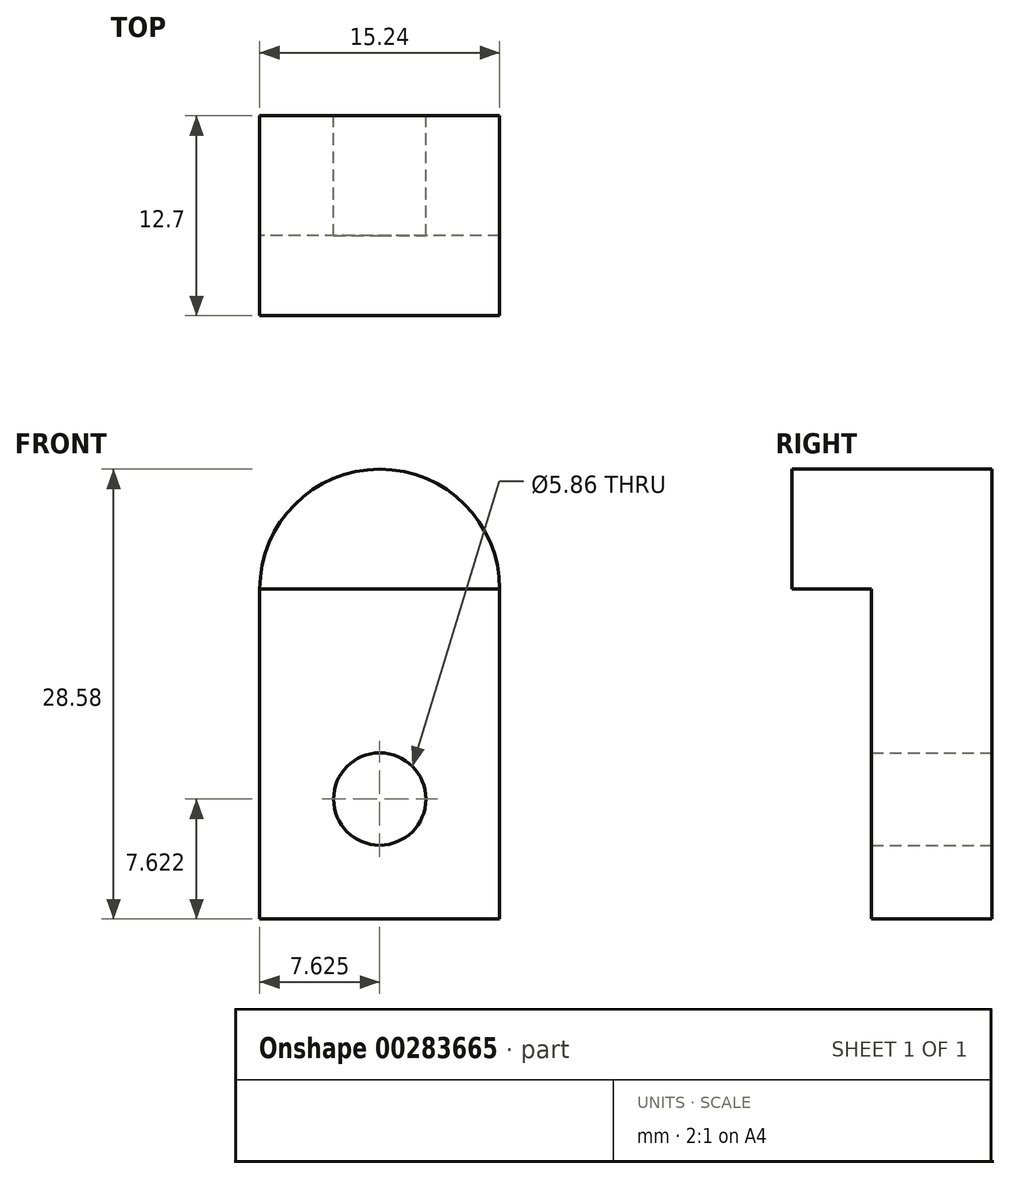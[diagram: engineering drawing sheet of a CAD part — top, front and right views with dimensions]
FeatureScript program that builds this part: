
annotation { "Feature Type Name" : "Feature", "Feature Type Description" : "" }
export const myFeature = defineFeature(function(context is Context, id is Id, definition is map)
    precondition{}
    {
        {
            var Q0;
            Q0=qCreatedBy(makeId("Front.planeOp"),FACE);
            var sketch = newSketch(context, id + "F0", { "sketchPlane" : qUnion([Q0])});
            skLineSegment(sketch, "E0.bottom", {"start": v(-29.2, 25.8) * mm, "end": v(-13.97, 25.8) * mm});
            skLineSegment(sketch, "E0.top", {"start": v(-29.2, 4.85) * mm, "end": v(-13.97, 4.85) * mm});
            skLineSegment(sketch, "E0.left", {"start": v(-29.2, 25.8) * mm, "end": v(-29.2, 4.85) * mm});
            skLineSegment(sketch, "E0.right", {"start": v(-13.97, 25.8) * mm, "end": v(-13.97, 4.85) * mm});
            skArc(sketch, "E1", {"start": v(-13.97, 25.8) * mm, "mid": v(-21.59, 33.43) * mm, "end": v(-29.2, 25.8) * mm});
            skCircle(sketch, "E2", {"center": v(-21.59, 12.47) * mm, "radius": 2.93 * mm});
            skSolve(sketch);
        }
        {
            var Q0;
            Q0 = qSketchRegion(id + "F0", true);
            extrude(context, id + "F1", {"entities" : qUnion([Q0]), "depth" : 7.62 * mm});
        }
        {
            var Q0;
            Q0=makeQuery(id+"F0.imprint","IMPRINT",FACE,{"disambiguationData":[TD([[makeQuery(id+"F0.imprint","IMPRINT",EDGE,{"derivedFrom":sQuery(id+"F0.wireOp",EDGE,"E0.bottom")}),1.0]])]});
            extrude(context, id + "F2", {"entities" : qUnion([Q0]), "operationType" : NewBodyOperationType.ADD, "depth" : 12.7 * mm});
        }
    });
